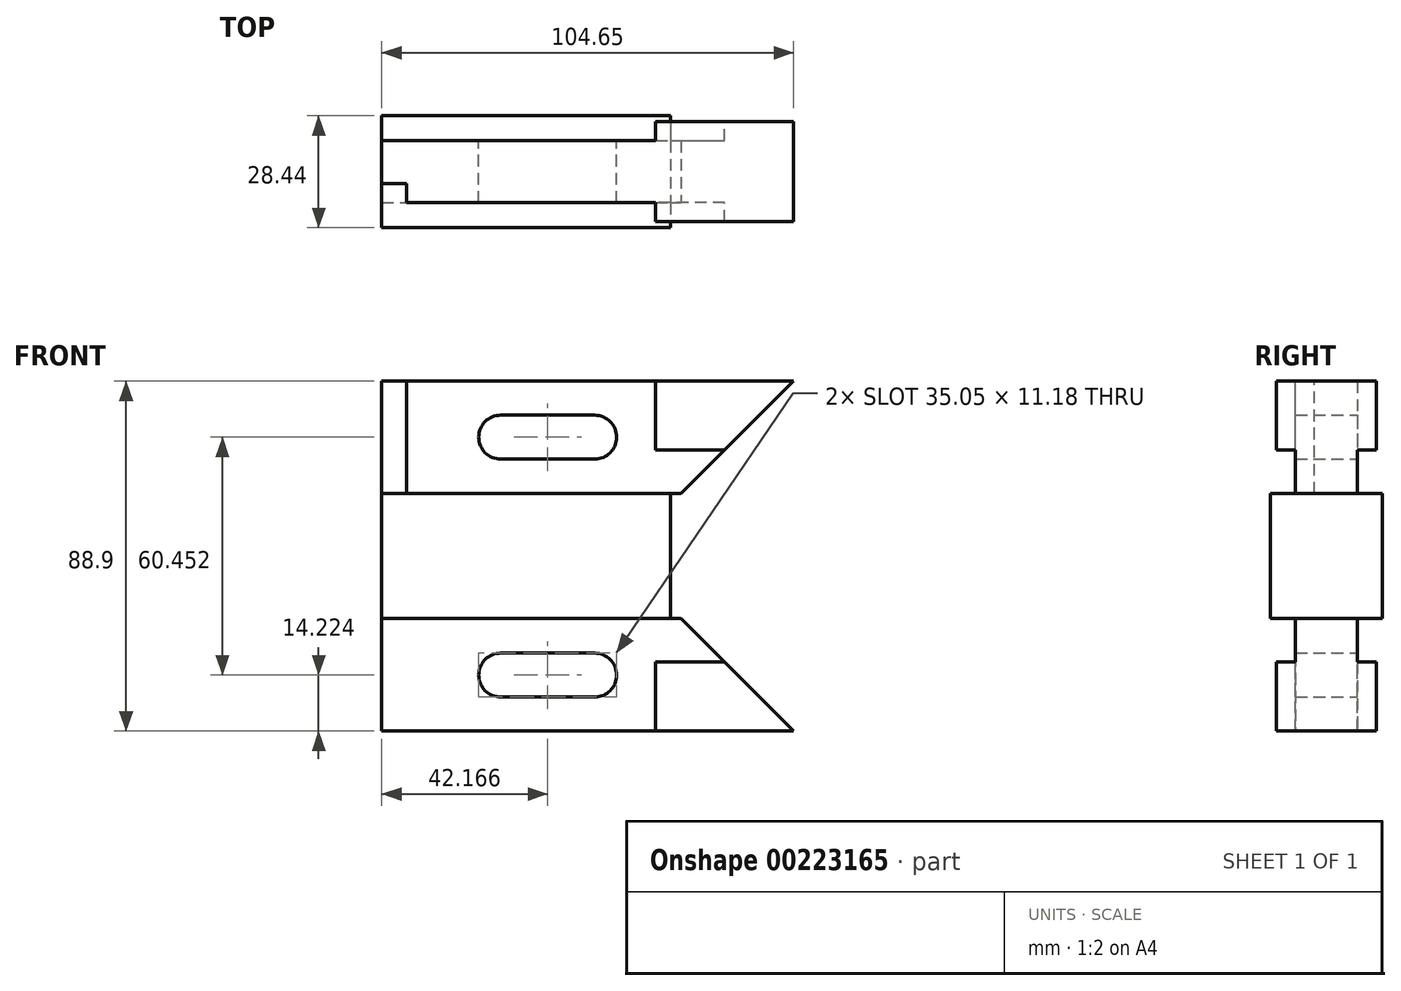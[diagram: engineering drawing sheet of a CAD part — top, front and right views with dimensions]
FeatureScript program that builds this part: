
annotation { "Feature Type Name" : "Feature", "Feature Type Description" : "" }
export const myFeature = defineFeature(function(context is Context, id is Id, definition is map)
    precondition{}
    {
        {
            var Q0;
            Q0=qCreatedBy(makeId("Right.planeOp"),FACE);
            var sketch = newSketch(context, id + "F0", { "sketchPlane" : qUnion([Q0])});
            skLineSegment(sketch, "E0", {"start": v(-14.22, 0) * mm, "end": v(14.22, 0) * mm, "construction": true});
            skLineSegment(sketch, "E1", {"start": v(-14.22, 0) * mm, "end": v(-14.22, 15.88) * mm});
            skLineSegment(sketch, "E2", {"start": v(-7.87, 15.88) * mm, "end": v(-7.87, 44.45) * mm});
            skLineSegment(sketch, "E3", {"start": v(7.87, 15.88) * mm, "end": v(14.22, 15.88) * mm});
            skLineSegment(sketch, "E4", {"start": v(14.22, 0) * mm, "end": v(14.22, 15.88) * mm});
            skLineSegment(sketch, "E5", {"start": v(-7.87, 44.45) * mm, "end": v(7.87, 44.45) * mm});
            skLineSegment(sketch, "E6", {"start": v(7.87, 44.45) * mm, "end": v(7.87, 15.88) * mm});
            skLineSegment(sketch, "E7", {"start": v(-14.22, 15.88) * mm, "end": v(-7.87, 15.88) * mm});
            skLineSegment(sketch, "E8.MirrorCS", {"start": v(14.22, 0) * mm, "end": v(14.22, -15.88) * mm});
            skLineSegment(sketch, "E9.MirrorCS", {"start": v(-14.22, 0) * mm, "end": v(-14.22, -15.88) * mm});
            skLineSegment(sketch, "E10.MirrorCS", {"start": v(-14.22, -15.88) * mm, "end": v(-7.87, -15.88) * mm});
            skLineSegment(sketch, "E11.MirrorCS", {"start": v(7.87, -15.88) * mm, "end": v(14.22, -15.88) * mm});
            skLineSegment(sketch, "E12.MirrorCS", {"start": v(7.87, -44.45) * mm, "end": v(7.87, -15.88) * mm});
            skLineSegment(sketch, "E13.MirrorCS", {"start": v(-7.87, -15.88) * mm, "end": v(-7.87, -44.45) * mm});
            skLineSegment(sketch, "E14.MirrorCS", {"start": v(-7.87, -44.45) * mm, "end": v(7.87, -44.45) * mm});
            skSolve(sketch);
        }
        {
            var Q0;
            Q0 = qSketchRegion(id + "F0", true);
            extrude(context, id + "F1", {"entities" : qUnion([Q0]), "oppositeDirection" : true, "depth" : 104.65 * mm});
        }
        {
            var Q0;
            Q0=makeQuery(id+"F1.opExtrude","SWEPT_FACE",FACE,{"disambiguationData":[OSD([sQuery(id+"F0.wireOp",EDGE,"E5")])]});
            var sketch = newSketch(context, id + "F2", { "sketchPlane" : qUnion([Q0])});
            skLineSegment(sketch, "E15.bottom", {"start": v(-104.65, -7.87) * mm, "end": v(-98.3, -7.87) * mm});
            skLineSegment(sketch, "E15.top", {"start": v(-104.65, -3.05) * mm, "end": v(-98.3, -3.05) * mm});
            skLineSegment(sketch, "E15.left", {"start": v(-104.65, -7.87) * mm, "end": v(-104.65, -3.05) * mm});
            skLineSegment(sketch, "E16", {"start": v(-98.3, -3.05) * mm, "end": v(-98.3, -7.87) * mm});
            skSolve(sketch);
        }
        {
            var Q0;
            Q0 = qSketchRegion(id + "F2", true);
            var Q1;
            Q1=makeQuery(id+"F1.opExtrude","SWEPT_FACE",FACE,{"disambiguationData":[OSD([sQuery(id+"F0.wireOp",EDGE,"E7")])]});
            extrude(context, id + "F3", {"entities" : qUnion([Q0]), "operationType" : NewBodyOperationType.REMOVE, "endBound" : BoundingType.UP_TO_SURFACE, "oppositeDirection" : true, "endBoundEntityFace" : qUnion([Q1]), "depth" : 25.4 * mm});
        }
        {
            var Q0;
            Q0=qCreatedBy(makeId("Front.planeOp"),FACE);
            var sketch = newSketch(context, id + "F4", { "sketchPlane" : qUnion([Q0])});
            skLineSegment(sketch, "E17", {"start": v(0, 0) * mm, "end": v(-107.27, 0) * mm, "construction": true});
            skArc(sketch, "E18", {"start": v(-74.42, -24.64) * mm, "mid": v(-80.01, -30.23) * mm, "end": v(-74.42, -35.81) * mm});
            skArc(sketch, "E19", {"start": v(-50.55, -35.81) * mm, "mid": v(-44.96, -30.23) * mm, "end": v(-50.55, -24.64) * mm});
            skLineSegment(sketch, "E20", {"start": v(-74.42, -24.64) * mm, "end": v(-50.55, -24.64) * mm});
            skLineSegment(sketch, "E21", {"start": v(-74.42, -35.81) * mm, "end": v(-50.55, -35.81) * mm});
            skLineSegment(sketch, "E22.MirrorCS", {"start": v(-74.42, 24.64) * mm, "end": v(-50.55, 24.64) * mm});
            skArc(sketch, "E23.MirrorCS", {"start": v(-50.55, 35.81) * mm, "mid": v(-44.96, 30.23) * mm, "end": v(-50.55, 24.64) * mm});
            skLineSegment(sketch, "E24.MirrorCS", {"start": v(-74.42, 35.81) * mm, "end": v(-50.55, 35.81) * mm});
            skArc(sketch, "E25.MirrorCS", {"start": v(-74.42, 24.64) * mm, "mid": v(-80.01, 30.23) * mm, "end": v(-74.42, 35.81) * mm});
            skSolve(sketch);
        }
        {
            var Q0;
            Q0 = qSketchRegion(id + "F4", true);
            extrude(context, id + "F5", {"entities" : qUnion([Q0]), "operationType" : NewBodyOperationType.REMOVE, "endBound" : BoundingType.SYMMETRIC, "depth" : 137.16 * mm});
        }
        {
            var Q0;
            Q0=qCreatedBy(makeId("Front.planeOp"),FACE);
            var sketch = newSketch(context, id + "F6", { "sketchPlane" : qUnion([Q0])});
            skLineSegment(sketch, "E26", {"start": v(0, 0) * mm, "end": v(-121.21, 0) * mm, "construction": true});
            skPoint(sketch, "E27.0", {"position": v(-101.47, 44.45) * mm});
            skLineSegment(sketch, "E28.0", {"start": v(-104.65, 44.45) * mm, "end": v(-98.3, 44.45) * mm});
            skLineSegment(sketch, "E29.0", {"start": v(-104.65, 15.87) * mm, "end": v(-104.65, 44.45) * mm});
            skLineSegment(sketch, "E30.0", {"start": v(-104.65, -15.88) * mm, "end": v(-104.65, 15.88) * mm});
            skLineSegment(sketch, "E31", {"start": v(-104.65, 44.45) * mm, "end": v(-35.05, 44.45) * mm});
            skLineSegment(sketch, "E32", {"start": v(-35.05, 44.45) * mm, "end": v(-35.05, 26.92) * mm});
            skLineSegment(sketch, "E33", {"start": v(-35.05, 44.45) * mm, "end": v(0, 44.45) * mm});
            skLineSegment(sketch, "E34", {"start": v(-35.05, 26.92) * mm, "end": v(-17.53, 26.92) * mm});
            skLineSegment(sketch, "E35", {"start": v(-17.53, 26.92) * mm, "end": v(0, 44.45) * mm});
            skLineSegment(sketch, "E36.MirrorCS", {"start": v(-17.53, -26.92) * mm, "end": v(0, -44.45) * mm});
            skLineSegment(sketch, "E37.MirrorCS", {"start": v(-35.05, -26.92) * mm, "end": v(-17.53, -26.92) * mm});
            skLineSegment(sketch, "E38.MirrorCS", {"start": v(-35.05, -44.45) * mm, "end": v(-35.05, -26.92) * mm});
            skLineSegment(sketch, "E39.MirrorCS", {"start": v(-35.05, -44.45) * mm, "end": v(0, -44.45) * mm});
            skSolve(sketch);
        }
        {
            var Q0;
            Q0 = qSketchRegion(id + "F6", true);
            extrude(context, id + "F7", {"entities" : qUnion([Q0]), "endBound" : BoundingType.SYMMETRIC, "depth" : 25.4 * mm});
        }
        {
            var Q0;
            Q0=makeQuery(id+"F7.opExtrude","SWEPT_BODY",BODY,{"disambiguationData":[OSD([sQuery(id+"F6.wireOp",EDGE,"E36.MirrorCS"),sQuery(id+"F6.wireOp",EDGE,"E37.MirrorCS"),sQuery(id+"F6.wireOp",EDGE,"E38.MirrorCS"),sQuery(id+"F6.wireOp",EDGE,"E39.MirrorCS")])]});
            var Q1;
            Q1=makeQuery(id+"F7.opExtrude","SWEPT_BODY",BODY,{"disambiguationData":[OSD([sQuery(id+"F6.wireOp",EDGE,"E32"),sQuery(id+"F6.wireOp",EDGE,"E33"),sQuery(id+"F6.wireOp",EDGE,"E34"),sQuery(id+"F6.wireOp",EDGE,"E35")])]});
            var Q2;
            Q2=makeQuery(id+"F1.opExtrude","SWEPT_BODY",BODY,{"disambiguationData":[OSD([sQuery(id+"F0.wireOp",EDGE,"E1"),sQuery(id+"F0.wireOp",EDGE,"E2"),sQuery(id+"F0.wireOp",EDGE,"E3"),sQuery(id+"F0.wireOp",EDGE,"E4"),sQuery(id+"F0.wireOp",EDGE,"E5"),sQuery(id+"F0.wireOp",EDGE,"E6"),sQuery(id+"F0.wireOp",EDGE,"E7"),sQuery(id+"F0.wireOp",EDGE,"E8.MirrorCS"),sQuery(id+"F0.wireOp",EDGE,"E9.MirrorCS"),sQuery(id+"F0.wireOp",EDGE,"E10.MirrorCS"),sQuery(id+"F0.wireOp",EDGE,"E11.MirrorCS"),sQuery(id+"F0.wireOp",EDGE,"E12.MirrorCS"),sQuery(id+"F0.wireOp",EDGE,"E13.MirrorCS"),sQuery(id+"F0.wireOp",EDGE,"E14.MirrorCS")])]});
            booleanBodies(context, id + "F8", {"operationType" : BooleanOperationType.UNION, "tools" : qUnion([Q0, Q1, Q2])});
        }
        {
            var Q0;
            Q0=qCreatedBy(makeId("Front.planeOp"),FACE);
            var sketch = newSketch(context, id + "F9", { "sketchPlane" : qUnion([Q0])});
            skLineSegment(sketch, "E40.0", {"start": v(-104.65, 15.88) * mm, "end": v(0, 15.88) * mm});
            skLineSegment(sketch, "E41.0.0", {"start": v(0, -15.88) * mm, "end": v(0, 15.88) * mm});
            skLineSegment(sketch, "E41.0.2", {"start": v(-104.65, 15.88) * mm, "end": v(-104.65, -15.88) * mm});
            skLineSegment(sketch, "E41.0.3", {"start": v(-104.65, -15.88) * mm, "end": v(0, -15.88) * mm});
            skLineSegment(sketch, "E42.0.0", {"start": v(-104.65, -44.45) * mm, "end": v(-35.05, -44.45) * mm});
            skLineSegment(sketch, "E42.0.1", {"start": v(-35.05, -44.45) * mm, "end": v(-35.05, -26.92) * mm});
            skLineSegment(sketch, "E42.0.2", {"start": v(-35.05, -26.92) * mm, "end": v(-17.53, -26.92) * mm});
            skLineSegment(sketch, "E42.0.3", {"start": v(-17.53, -26.92) * mm, "end": v(0, -44.45) * mm});
            skLineSegment(sketch, "E42.0.4", {"start": v(0, -44.45) * mm, "end": v(0, -15.88) * mm});
            skLineSegment(sketch, "E42.0.5", {"start": v(0, -15.88) * mm, "end": v(-104.65, -15.88) * mm});
            skLineSegment(sketch, "E42.0.6", {"start": v(-104.65, -15.88) * mm, "end": v(-104.65, -44.45) * mm});
            skLineSegment(sketch, "E43.0.0", {"start": v(-35.05, -26.92) * mm, "end": v(-35.05, -44.45) * mm});
            skLineSegment(sketch, "E43.0.1", {"start": v(-35.05, -44.45) * mm, "end": v(0, -44.45) * mm});
            skLineSegment(sketch, "E43.0.2", {"start": v(0, -44.45) * mm, "end": v(-17.53, -26.92) * mm});
            skLineSegment(sketch, "E43.0.3", {"start": v(-17.53, -26.92) * mm, "end": v(-35.05, -26.92) * mm});
            skLineSegment(sketch, "E44", {"start": v(-28.58, -15.88) * mm, "end": v(0, -15.88) * mm});
            skSolve(sketch);
        }
        {
            var Q0;
            Q0=qCreatedBy(makeId("Front.planeOp"),FACE);
            var sketch = newSketch(context, id + "F10", { "sketchPlane" : qUnion([Q0])});
            skLineSegment(sketch, "E45.0", {"start": v(-17.53, 26.92) * mm, "end": v(0, 44.45) * mm});
            skLineSegment(sketch, "E46.0", {"start": v(-17.53, -26.92) * mm, "end": v(0, -44.45) * mm});
            skLineSegment(sketch, "E47.0", {"start": v(0, -15.88) * mm, "end": v(-104.65, -15.88) * mm});
            skLineSegment(sketch, "E48.0", {"start": v(-104.65, 15.88) * mm, "end": v(0, 15.88) * mm});
            skLineSegment(sketch, "E49", {"start": v(0, 44.45) * mm, "end": v(-28.58, 15.88) * mm});
            skLineSegment(sketch, "E50", {"start": v(0, 15.88) * mm, "end": v(0, 44.45) * mm});
            skLineSegment(sketch, "E51", {"start": v(0, 15.88) * mm, "end": v(-28.58, 15.88) * mm});
            skLineSegment(sketch, "E52", {"start": v(0, -44.45) * mm, "end": v(-28.58, -15.87) * mm});
            skLineSegment(sketch, "E53", {"start": v(0, -44.45) * mm, "end": v(0, -15.88) * mm});
            skSolve(sketch);
        }
        {
            var Q0;
            Q0 = qSketchRegion(id + "F10", true);
            extrude(context, id + "F11", {"entities" : qUnion([Q0]), "operationType" : NewBodyOperationType.REMOVE, "endBound" : BoundingType.SYMMETRIC, "oppositeDirection" : true, "depth" : 78.23 * mm});
        }
        {
            var Q0;
            Q0=qCreatedBy(makeId("Front.planeOp"),FACE);
            var sketch = newSketch(context, id + "F12", { "sketchPlane" : qUnion([Q0])});
            skLineSegment(sketch, "E54.0", {"start": v(0, -15.88) * mm, "end": v(0, 15.88) * mm});
            skLineSegment(sketch, "E55", {"start": v(0, 15.88) * mm, "end": v(0, -15.88) * mm});
            skLineSegment(sketch, "E56", {"start": v(0, 15.88) * mm, "end": v(-31.24, 15.88) * mm});
            skLineSegment(sketch, "E57", {"start": v(0, -15.88) * mm, "end": v(-31.24, -15.88) * mm});
            skLineSegment(sketch, "E58", {"start": v(-31.24, 15.88) * mm, "end": v(-31.24, -15.88) * mm});
            skSolve(sketch);
        }
        {
            var Q0;
            Q0 = qSketchRegion(id + "F12", true);
            extrude(context, id + "F13", {"entities" : qUnion([Q0]), "operationType" : NewBodyOperationType.REMOVE, "endBound" : BoundingType.SYMMETRIC, "oppositeDirection" : true, "depth" : 134.62 * mm});
        }
    });
